# Revit family: 151_HL317H
name_source: partatom
category: Instalační zařizovací předměty
revit_build: Autodesk Revit 2016 (Build: 20151007_0715(x64)
units: mm (PartAtom-declared; Revit-internal decimal feet)

## family parameters
Bod výpočtu místnosti = Ano
Kóta kulaté spojky = Použít průměr
Nadpis OmniClass = Deck Waste Water Drains
Ořezat dutým tvarem při načtení = Ne
Sdílené = Ano
Typ součásti = Normální
Vždy vertikální = Ano
Založené na pracovní rovině = Ne
Číslo OmniClass = 23.70.50.21.24.14

## types (1)
- HL317H
    EAN = 9003076317110
    Klíčová poznámka = HL317H
    Komentáře k typům = HL317H Трап для внутренних помещенийDN50/75/110 вертикальный с приварным полимербитумным полотном, 147х147мм/138х138мм
    Model = HL317H
    Popis = Трапы для внутренних помещений
    Připojení CW = Ne
    Připojení HW = Ne
    Připojení odpadu = Ano
    Připojení ventilace = Ne
    URL = http://www.hutterer-lechner.com
    Výrobce = HL Hutterer & Lechner GmbH
    ВЕС = 1,98 [kg]
    ВЫСОТА МОНТАЖА = 220 mm
    МАКСИМАЛЬНАЯ НАГРУЗКА КЛАССА = K3 - 300kg
    МАТЕРИАЛ = PP
    НАСАДКА = 20-70 mm / 147 x 147 mm / PP
    ПРОИЗВОДИТЕЛЬНОСТЬ = 1,8 l/s
    ПРОПУСКНАЯ СПОСОБНОСТЬ = 1.8 L/s
    РАЗМЕР = DN50/75/110
    РЕШЁТКА = 138 x 138 mm / V2A

## geometry (parser evidence)
native form markers: Sweep x17
no freeform markers — native parametric forms only
